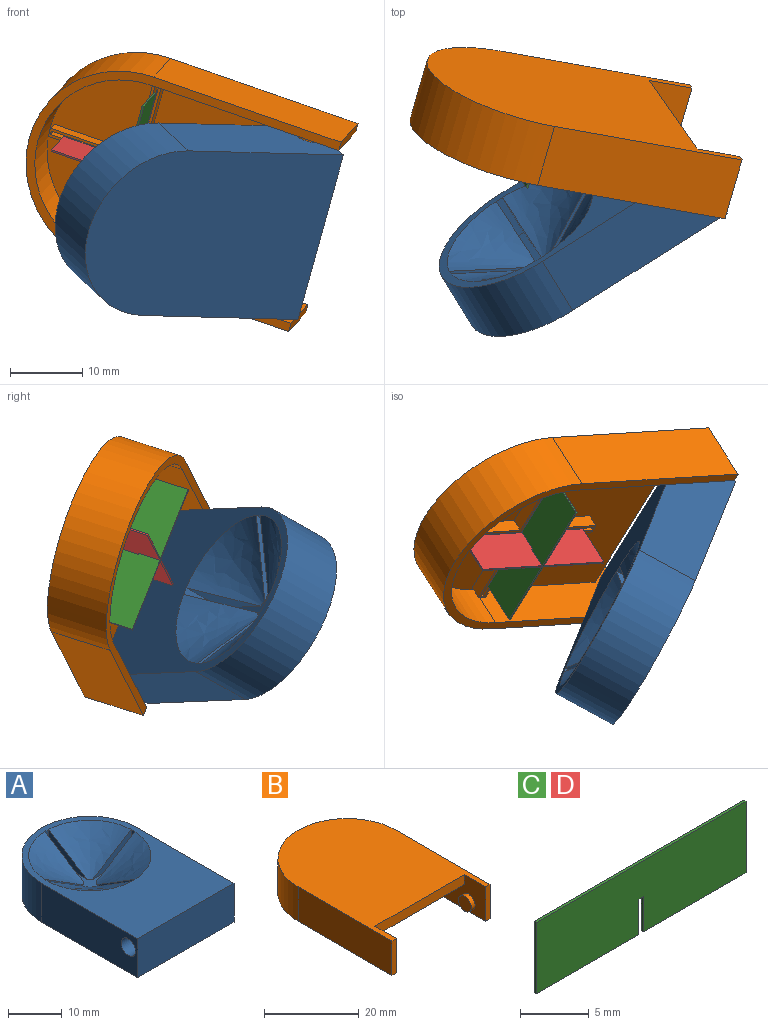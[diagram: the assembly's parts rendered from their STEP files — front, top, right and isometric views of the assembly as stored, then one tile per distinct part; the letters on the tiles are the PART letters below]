
ASSEMBLY  parts=4 mates=3
PART A: 24 faces, bbox 25.4x38.1x8.9 mm
  f0: bspline ~11.38x11.33mm, area 107.3mm2, adj f7,f9,f19,f21
  f1: bspline ~11.38x11.33mm, area 107.3mm2, adj f7,f12,f17,f21
  f2: bspline ~11.38x11.33mm, area 107.3mm2, adj f7,f11,f13,f21
  f3: plane 25.4x8.89mm, normal (-1,0,0), area 214.4mm2, adj f4,f6,f7,f22,f23
  f4: plane 25.4x8.89mm, normal (0,-1,0), area 225.8mm2, adj f3,f5,f7,f22
  f5: plane 25.4x8.89mm, normal (1,0,0), area 214.4mm2, adj f4,f6,f7,f22,f23
  f6: cylinder r=12.7mm len=25.4mm, axis (0,0,-1), area 354.7mm2, adj f3,f5,f7,f22
  f7: plane 38.14x25.44mm, normal (0,0,1), area 488.1mm2, adj f0,f1,f2,f3,f4,f5,f6,f8
  f8: bspline ~11.38x11.33mm, area 107.3mm2, adj f7,f16,f20,f21
  f9: plane 10.25x6.35mm, normal (0,-1,0), area 32.4mm2, adj f0,f10,f21
  f10: cylinder r=11.43mm len=6.35mm, axis (0,0,-1), area 6.5mm2, adj f7,f9,f11,f21
  f11: plane 10.25x6.35mm, normal (0,1,0), area 32.4mm2, adj f2,f10,f21
  f12: plane 10.25x6.35mm, normal (-1,0,0), area 32.4mm2, adj f1,f14,f21
  f13: plane 10.25x6.35mm, normal (1,0,0), area 32.4mm2, adj f2,f14,f21
  f14: cylinder r=11.43mm len=6.35mm, axis (0,0,-1), area 6.5mm2, adj f7,f12,f13,f21
  f15: cylinder r=11.43mm len=6.35mm, axis (0,0,-1), area 6.5mm2, adj f7,f16,f17,f21
  f16: plane 10.25x6.35mm, normal (0,-1,0), area 32.4mm2, adj f8,f15,f21
  f17: plane 10.25x6.35mm, normal (0,1,0), area 32.4mm2, adj f1,f15,f21
  f18: cylinder r=11.43mm len=6.35mm, axis (0,0,-1), area 6.5mm2, adj f7,f19,f20,f21
  f19: plane 10.25x6.35mm, normal (1,0,0), area 32.4mm2, adj f0,f18,f21
  f20: plane 10.25x6.35mm, normal (-1,0,0), area 32.4mm2, adj f8,f18,f21
  f21: plane 22.86x22.86mm, normal (0,0,1), area 46.5mm2, adj f0,f1,f2,f8,f9,f10,f11,f12
  f22: plane 38.1x25.4mm, normal (0,0,-1), area 898.5mm2, adj f3,f4,f5,f6
  f23: cylinder r=1.91mm len=25.4mm, axis (1,0,0), area 304mm2, adj f3,f5
PART B: 42 faces, bbox 29.2x42.5x8.9 mm
  f0: cylinder r=1.91mm len=3.81mm, axis (-1,0,0), area 13.7mm2, adj f7,f41
  f1: plane 34.93x26.67mm, normal (0,0,-1), area 791.3mm2, adj f7,f8,f9,f12,f24,f25,f26,f27
  f2: plane 42.55x29.21mm, normal (0,0,-1), area 126.7mm2, adj f3,f4,f5,f6,f7,f9,f10,f12
  f3: plane 27.94x8.89mm, normal (1,0,0), area 248.4mm2, adj f2,f4,f10,f11
  f4: cylinder r=14.61mm len=29.21mm, axis (0,0,-1), area 407.9mm2, adj f2,f3,f5,f11
  f5: plane 27.94x8.89mm, normal (-1,0,0), area 248.4mm2, adj f2,f4,f6,f11
  f6: plane 8.89x1.27mm, normal (0,-1,0), area 11.3mm2, adj f2,f5,f7,f11
  f7: plane 27.94x8.89mm, normal (1,0,0), area 182.1mm2, adj f0,f1,f2,f6,f8,f11,f12
  f8: plane 26.67x2.54mm, normal (0,-1,0), area 67.7mm2, adj f1,f7,f9,f11
  f9: plane 27.94x8.89mm, normal (-1,0,0), area 182.1mm2, adj f1,f2,f8,f10,f11,f12,f39
  f10: plane 8.89x1.27mm, normal (0,-1,0), area 11.3mm2, adj f2,f3,f9,f11
  f11: plane 42.55x29.21mm, normal (0,0,1), area 981.8mm2, adj f3,f4,f5,f6,f7,f8,f9,f10
  f12: cylinder r=13.33mm len=26.67mm, axis (0,0,-1), area 266mm2, adj f1,f2,f7,f9
  f13: plane 12.45x1.91mm, normal (-1,0,0), area 23.7mm2, adj f14,f36,f37,f38
  f14: plane 1.91x0.51mm, normal (0,1,0), area 1mm2, adj f13,f15,f37,f38
  f15: plane 12.45x1.91mm, normal (1,0,0), area 23.7mm2, adj f14,f16,f37,f38
  f16: plane 12.45x1.91mm, normal (0,1,0), area 23.7mm2, adj f15,f17,f37,f38
  f17: plane 1.91x0.51mm, normal (1,0,0), area 1mm2, adj f16,f18,f37,f38
  f18: plane 12.45x1.91mm, normal (0,-1,0), area 23.7mm2, adj f17,f19,f37,f38
  f19: plane 12.45x1.91mm, normal (1,0,0), area 23.7mm2, adj f18,f20,f37,f38
  f20: plane 1.91x0.51mm, normal (0,-1,0), area 1mm2, adj f19,f21,f37,f38
  f21: plane 12.45x1.91mm, normal (-1,0,0), area 23.7mm2, adj f20,f22,f37,f38
  f22: plane 12.45x1.91mm, normal (0,-1,0), area 23.7mm2, adj f21,f23,f37,f38
  f23: plane 1.91x0.51mm, normal (-1,0,0), area 1mm2, adj f22,f36,f37,f38
  f24: plane 12.26x1.91mm, normal (-1,0,0), area 23.3mm2, adj f1,f25,f35,f37
  f25: plane 1.91x1.27mm, normal (0,-1,0), area 2.4mm2, adj f1,f24,f26,f37
  f26: plane 12.26x1.91mm, normal (1,0,0), area 23.3mm2, adj f1,f25,f27,f37
  f27: plane 12.26x1.91mm, normal (0,-1,0), area 23.3mm2, adj f1,f26,f28,f37
  f28: plane 1.91x1.27mm, normal (1,0,0), area 2.4mm2, adj f1,f27,f29,f37
  f29: plane 12.26x1.91mm, normal (0,1,0), area 23.3mm2, adj f1,f28,f30,f37
  f30: plane 12.26x1.91mm, normal (1,0,0), area 23.3mm2, adj f1,f29,f31,f37
  f31: plane 1.91x1.27mm, normal (0,1,0), area 2.4mm2, adj f1,f30,f32,f37
  f32: plane 12.26x1.91mm, normal (-1,0,0), area 23.3mm2, adj f1,f31,f33,f37
  f33: plane 12.26x1.91mm, normal (0,1,0), area 23.3mm2, adj f1,f32,f34,f37
  f34: plane 1.91x1.27mm, normal (-1,0,0), area 2.4mm2, adj f1,f33,f35,f37
  f35: plane 12.26x1.91mm, normal (0,-1,0), area 23.3mm2, adj f1,f24,f34,f37
  f36: plane 12.45x1.91mm, normal (0,1,0), area 23.7mm2, adj f13,f23,f37,f38
  f37: plane 25.78x25.78mm, normal (0,0,-1), area 38.3mm2, adj f13,f14,f15,f16,f17,f18,f19,f20
  f38: plane 25.4x25.4mm, normal (0,0,-1), area 25.5mm2, adj f13,f14,f15,f16,f17,f18,f19,f20
  f39: cylinder r=1.91mm len=3.81mm, axis (-1,0,0), area 13.7mm2, adj f9,f40
  f40: plane 3.81x3.81mm, normal (-1,0,0), area 11.4mm2, adj f39
  f41: plane 3.81x3.81mm, normal (1,0,0), area 11.4mm2, adj f0
PART C: 10 faces, bbox 21.6x0.3x6.4 mm
  f0: plane 10.54x0.25mm, normal (0,0,-1), area 2.7mm2, adj f1,f7,f8,f9
  f1: plane 6.35x0.25mm, normal (1,0,0), area 1.6mm2, adj f0,f2,f8,f9
  f2: plane 21.59x0.25mm, normal (0,0,1), area 5.5mm2, adj f1,f3,f8,f9
  f3: plane 6.35x0.25mm, normal (-1,0,0), area 1.6mm2, adj f2,f4,f8,f9
  f4: plane 10.54x0.25mm, normal (0,0,-1), area 2.7mm2, adj f3,f5,f8,f9
  f5: plane 3.18x0.25mm, normal (1,0,0), area 0.8mm2, adj f4,f6,f8,f9
  f6: plane 0.51x0.25mm, normal (0,0,-1), area 0.1mm2, adj f5,f7,f8,f9
  f7: plane 3.18x0.25mm, normal (-1,0,0), area 0.8mm2, adj f0,f6,f8,f9
  f8: plane 21.59x6.35mm, normal (0,-1,0), area 135.5mm2, adj f0,f1,f2,f3,f4,f5,f6,f7
  f9: plane 21.59x6.35mm, normal (0,1,0), area 135.5mm2, adj f0,f1,f2,f3,f4,f5,f6,f7
PART D: same geometry as C
PLACE A rot(axis=(-0.5,0.29,0.81),132.3deg) t=(-98.52,29.2,-77.67)mm
PLACE B rot(axis=(-0.32,0.63,0.7),113.3deg) t=(-102.67,45.31,-70.24)mm
PLACE C rot(axis=(0.57,0.61,-0.55),148.6deg) t=(-102.22,46.45,-69.91)mm
PLACE D rot(axis=(-0.95,0.31,0.04),73.1deg) t=(-102.37,46.52,-69.98)mm
MATE pin_slot B.f0 <-> A.f23  axis (-0.25,0.36,-0.9) through (-77.67,39.48,-65.93)mm
MATE fastened C.f6 <-> D.f6  axis (0.27,0.92,0.29) through (-102.34,46.48,-69.87)mm
MATE fastened D.f2 <-> B.f4  axis (0.27,0.92,0.29) through (-101.49,49.39,-68.94)mm
